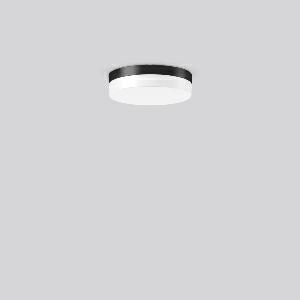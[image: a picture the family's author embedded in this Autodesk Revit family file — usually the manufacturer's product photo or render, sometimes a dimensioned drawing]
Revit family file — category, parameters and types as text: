
# Revit family: flat_slim_round_312132_0031_1_191_097a
name_source: partatom
category: Lighting Fixtures
units: mm (PartAtom-declared; Revit-internal decimal feet)

## family parameters
Cut with Voids When Loaded = No
Host = Face
Light Source = No
Part Type = Normal
Room Calculation Point = No
Round Connector Dimension = Use Diameter
Shared = No

## types (1)
- FLAT SLIM round (1 x LED Modul 840, 1000 lm, 4000)
    Apparent Load = 13 VA
    CIE Flux Codes = 42 72 92 89 100
    Color Rendering = 80
    Color Temperature = 4000
    Default Elevation = 1800 mm
    Height = 63 mm
    Lamp = 1 x LED Modul 840
    Lamp Light Flux = 1000 lm
    Lamp count = 1
    Length = 230 mm
    Lifetime = 50000 h
    Luminous efficacy = 77 lm/W
    Manufacturer = RZB
    ModVariant = No
    Model = 312132.0031.1.191
    Mounting Place = Ceiling, Wall
    Mounting Type = Surface mounted
    Number of Poles = 1
    OnlyDefault = Yes
    Power Factor = 1
    Product Name = FLAT SLIM round
    Product group = Surface mounted ceiling and wall luminaires
    ProductGroupID = 305
    Protection Class = Protection class I
    Protection Degree = IP 65
    RLX_Detail_Level = 1
    RLX_Emergency_Light_Flux = 0 lm
    RLX_Emergency_Type = 0
    RLX_Emergency_Type_DB = No
    RlxData = <blob elided: 17913 chars, md5=3747aa3c>
    Socket = socket
    Standby Power = 0 W
    System Light Flux = 1000 lm
    System Power = 13 W
    Type Comments = Product without accessories
    Type Image = 312132.0031.jpg
    URL = http://relux.com
    VarID = ---
    Voltage = 230 V
    Voltage Range = 220-240 V
    Weight = 0.00 kg
    Width = 0 mm  [stored 0 ft]

note: [stored X ft] marks values corroborated as IEEE doubles in the binary element streams (Revit-internal decimal feet)

## geometry (parser evidence)
native form markers: Blend x4, Sweep x12
no freeform markers — native parametric forms only
